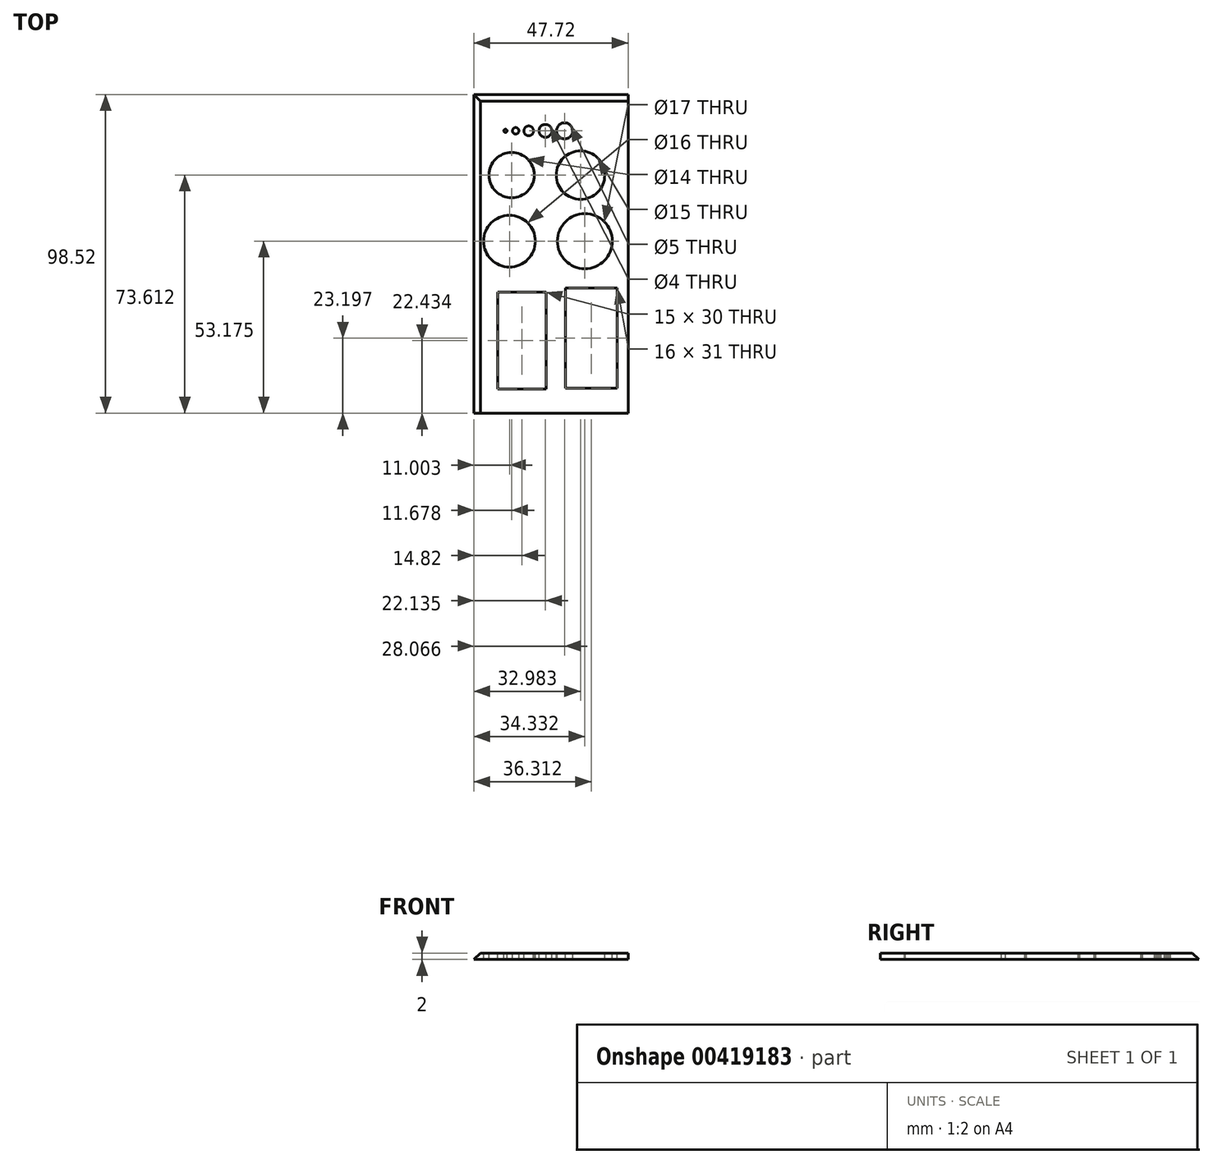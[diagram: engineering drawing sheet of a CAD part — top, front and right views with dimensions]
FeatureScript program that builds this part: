
annotation { "Feature Type Name" : "Feature", "Feature Type Description" : "" }
export const myFeature = defineFeature(function(context is Context, id is Id, definition is map)
    precondition{}
    {
        {
            var Q0;
            Q0=qCreatedBy(makeId("Top.planeOp"),FACE);
            var sketch = newSketch(context, id + "F0", { "sketchPlane" : qUnion([Q0])});
            skLineSegment(sketch, "E0.bottom", {"start": v(25.4, 50.8) * mm, "end": v(-25.4, 50.8) * mm});
            skLineSegment(sketch, "E0.top", {"start": v(25.4, -50.8) * mm, "end": v(-25.4, -50.8) * mm});
            skLineSegment(sketch, "E0.left", {"start": v(25.4, 50.8) * mm, "end": v(25.4, -50.8) * mm});
            skLineSegment(sketch, "E0.right", {"start": v(-25.4, 50.8) * mm, "end": v(-25.4, -50.8) * mm});
            skPoint(sketch, "E0.middle", {"position": v(0, 0) * mm});
            skSolve(sketch);
        }
        {
            var Q0;
            Q0=makeQuery(id+"F0.imprint","IMPRINT",FACE,{"disambiguationData":[TD([[makeQuery(id+"F0.imprint","IMPRINT",EDGE,{"derivedFrom":sQuery(id+"F0.wireOp",EDGE,"E0.bottom")}),1.0]])]});
            extrude(context, id + "F1", {"entities" : qUnion([Q0]), "depth" : 2 * mm});
        }
        {
            var Q0;
            Q0=makeQuery(id+"F1.opExtrude","CAP_EDGE",EDGE,{"disambiguationData":[OSD([sQuery(id+"F0.wireOp",EDGE,"E0.right")])],"isStart":false});
            var Q1;
            Q1=makeQuery(id+"F1.opExtrude","CAP_EDGE",EDGE,{"disambiguationData":[OSD([sQuery(id+"F0.wireOp",EDGE,"E0.bottom")])],"isStart":false});
            chamfer(context, id + "F2", {"entities" : qUnion([Q0, Q1]), "width" : 5.08 * mm, "tangentPropagation" : true});
        }
        {
            var Q0;
            Q0=makeQuery(id+"F1.opExtrude","CAP_FACE",FACE,{"disambiguationData":[OSD([sQuery(id+"F0.wireOp",EDGE,"E0.bottom"),sQuery(id+"F0.wireOp",EDGE,"E0.top"),sQuery(id+"F0.wireOp",EDGE,"E0.left"),sQuery(id+"F0.wireOp",EDGE,"E0.right")])],"isStart":false});
            var sketch = newSketch(context, id + "F3", { "sketchPlane" : qUnion([Q0])});
            skLineSegment(sketch, "E1", {"start": v(-20.32, 36.5) * mm, "end": v(25.4, 36.5) * mm, "construction": true});
            skCircle(sketch, "E2", {"center": v(-12.57, 36.5) * mm, "radius": 0.5 * mm});
            skCircle(sketch, "E3", {"center": v(-9.4, 36.5) * mm, "radius": 1 * mm});
            skCircle(sketch, "E4", {"center": v(-0.19, 36.5) * mm, "radius": 2 * mm});
            skCircle(sketch, "E5", {"center": v(-5.37, 36.5) * mm, "radius": 1.5 * mm});
            skCircle(sketch, "E6", {"center": v(5.75, 36.5) * mm, "radius": 2.5 * mm});
            skLineSegment(sketch, "E7", {"start": v(-20.32, 22.81) * mm, "end": v(25.4, 22.81) * mm, "construction": true});
            skCircle(sketch, "E8", {"center": v(-10.64, 22.81) * mm, "radius": 7 * mm});
            skCircle(sketch, "E9", {"center": v(10.66, 22.81) * mm, "radius": 7.5 * mm});
            skLineSegment(sketch, "E10", {"start": v(-20.32, 2.37) * mm, "end": v(25.4, 2.37) * mm, "construction": true});
            skCircle(sketch, "E11", {"center": v(-11.32, 2.37) * mm, "radius": 8 * mm});
            skCircle(sketch, "E12", {"center": v(12.01, 2.37) * mm, "radius": 8.5 * mm});
            skLineSegment(sketch, "E13.bottom", {"start": v(0, -13.37) * mm, "end": v(-15, -13.37) * mm});
            skLineSegment(sketch, "E13.top", {"start": v(0, -43.37) * mm, "end": v(-15, -43.37) * mm});
            skLineSegment(sketch, "E13.left", {"start": v(0, -13.37) * mm, "end": v(0, -43.37) * mm});
            skLineSegment(sketch, "E13.right", {"start": v(-15, -13.37) * mm, "end": v(-15, -43.37) * mm});
            skPoint(sketch, "E13.middle", {"position": v(-7.5, -28.37) * mm});
            skLineSegment(sketch, "E14.bottom", {"start": v(22, -12.1) * mm, "end": v(6, -12.1) * mm});
            skLineSegment(sketch, "E14.top", {"start": v(22, -43.1) * mm, "end": v(6, -43.1) * mm});
            skLineSegment(sketch, "E14.left", {"start": v(22, -12.1) * mm, "end": v(22, -43.1) * mm});
            skLineSegment(sketch, "E14.right", {"start": v(6, -12.1) * mm, "end": v(6, -43.1) * mm});
            skPoint(sketch, "E14.middle", {"position": v(14, -27.6) * mm});
            skSolve(sketch);
        }
        {
            var Q0;
            Q0=makeQuery(id+"F3.imprint","IMPRINT",FACE,{"disambiguationData":[TD([[makeQuery(id+"F3.imprint","IMPRINT",EDGE,{"derivedFrom":sQuery(id+"F3.wireOp",EDGE,"E13.bottom")}),1.0]])]});
            var Q1;
            Q1=makeQuery(id+"F3.imprint","IMPRINT",FACE,{"disambiguationData":[TD([[makeQuery(id+"F3.imprint","IMPRINT",EDGE,{"derivedFrom":sQuery(id+"F3.wireOp",EDGE,"E14.bottom")}),1.0]])]});
            var Q2;
            Q2=makeQuery(id+"F3.imprint","IMPRINT",FACE,{"disambiguationData":[TD([[makeQuery(id+"F3.imprint","IMPRINT",EDGE,{"derivedFrom":sQuery(id+"F3.wireOp",EDGE,"E12")}),1.0]])]});
            var Q3;
            Q3=makeQuery(id+"F3.imprint","IMPRINT",FACE,{"disambiguationData":[TD([[makeQuery(id+"F3.imprint","IMPRINT",EDGE,{"derivedFrom":sQuery(id+"F3.wireOp",EDGE,"E11")}),1.0]])]});
            var Q4;
            Q4=makeQuery(id+"F3.imprint","IMPRINT",FACE,{"disambiguationData":[TD([[makeQuery(id+"F3.imprint","IMPRINT",EDGE,{"derivedFrom":sQuery(id+"F3.wireOp",EDGE,"E8")}),1.0]])]});
            var Q5;
            Q5=makeQuery(id+"F3.imprint","IMPRINT",FACE,{"disambiguationData":[TD([[makeQuery(id+"F3.imprint","IMPRINT",EDGE,{"derivedFrom":sQuery(id+"F3.wireOp",EDGE,"E9")}),1.0]])]});
            var Q6;
            Q6=makeQuery(id+"F3.imprint","IMPRINT",FACE,{"disambiguationData":[TD([[makeQuery(id+"F3.imprint","IMPRINT",EDGE,{"derivedFrom":sQuery(id+"F3.wireOp",EDGE,"E6")}),1.0]])]});
            var Q7;
            Q7=makeQuery(id+"F3.imprint","IMPRINT",FACE,{"disambiguationData":[TD([[makeQuery(id+"F3.imprint","IMPRINT",EDGE,{"derivedFrom":sQuery(id+"F3.wireOp",EDGE,"E4")}),1.0]])]});
            var Q8;
            Q8=makeQuery(id+"F3.imprint","IMPRINT",FACE,{"disambiguationData":[TD([[makeQuery(id+"F3.imprint","IMPRINT",EDGE,{"derivedFrom":sQuery(id+"F3.wireOp",EDGE,"E5")}),1.0]])]});
            var Q9;
            Q9=makeQuery(id+"F3.imprint","IMPRINT",FACE,{"disambiguationData":[TD([[makeQuery(id+"F3.imprint","IMPRINT",EDGE,{"derivedFrom":sQuery(id+"F3.wireOp",EDGE,"E3")}),1.0]])]});
            var Q10;
            Q10=makeQuery(id+"F3.imprint","IMPRINT",FACE,{"disambiguationData":[TD([[makeQuery(id+"F3.imprint","IMPRINT",EDGE,{"derivedFrom":sQuery(id+"F3.wireOp",EDGE,"E2")}),1.0]])]});
            extrude(context, id + "F4", {"entities" : qUnion([Q0, Q1, Q2, Q3, Q4, Q5, Q6, Q7, Q8, Q9, Q10]), "operationType" : NewBodyOperationType.REMOVE, "oppositeDirection" : true, "depth" : 25.4 * mm});
        }
    });
